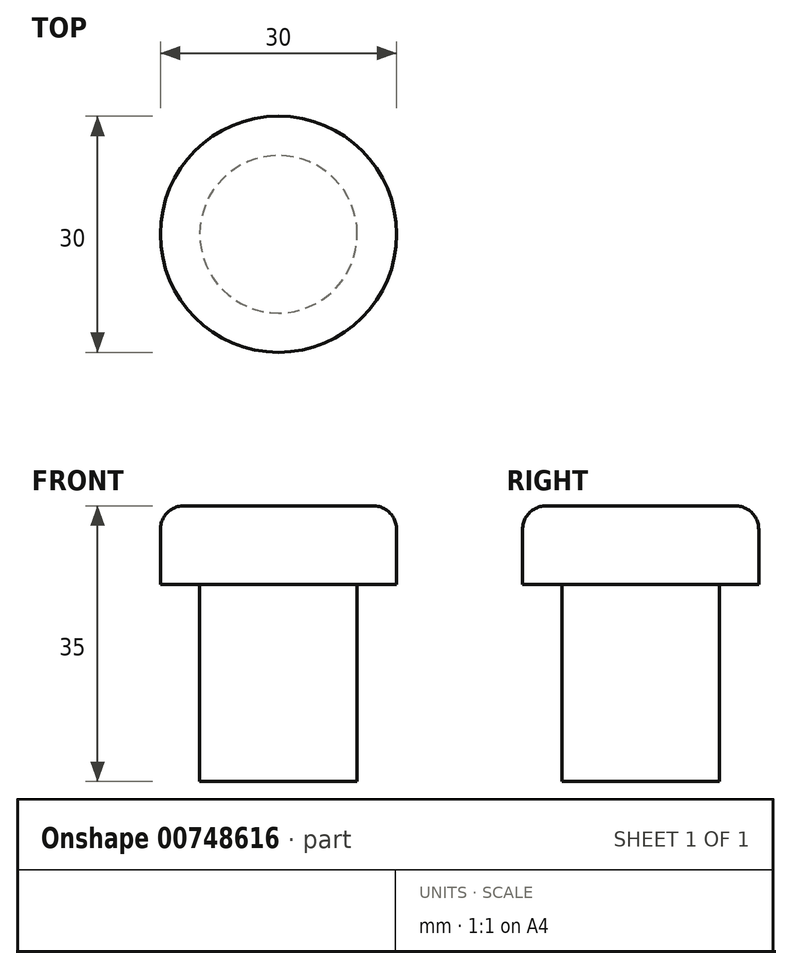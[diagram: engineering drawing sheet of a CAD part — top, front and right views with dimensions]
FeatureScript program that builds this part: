
annotation { "Feature Type Name" : "Feature", "Feature Type Description" : "" }
export const myFeature = defineFeature(function(context is Context, id is Id, definition is map)
    precondition{}
    {
        {
            var Q0;
            Q0=qCreatedBy(makeId("Top.planeOp"),FACE);
            var sketch = newSketch(context, id + "F0", { "sketchPlane" : qUnion([Q0])});
            skCircle(sketch, "E0", {"center": v(0, 0) * mm, "radius": 10 * mm});
            skSolve(sketch);
        }
        {
            var Q0;
            Q0=qSketchRegion(id+"F0",true);
            extrude(context, id + "F1", {"entities" : qUnion([Q0]), "depth" : 25 * mm, "offsetDistance" : 25 * mm});
        }
        {
            var Q0;
            Q0=makeQuery(id+"F1.opExtrude","CAP_FACE",FACE,{"disambiguationData":[OSD([sQuery(id+"F0.wireOp",EDGE,"E0")])],"isStart":false});
            var sketch = newSketch(context, id + "F2", { "sketchPlane" : qUnion([Q0])});
            skCircle(sketch, "E1", {"center": v(0, 0) * mm, "radius": 15 * mm});
            skSolve(sketch);
        }
        {
            var Q0;
            Q0=qSketchRegion(id+"F2",true);
            extrude(context, id + "F3", {"entities" : qUnion([Q0]), "operationType" : NewBodyOperationType.ADD, "depth" : 10 * mm, "offsetDistance" : 25 * mm});
        }
        {
            var Q0;
            Q0=makeQuery(id+"F3.opExtrude","CAP_EDGE",EDGE,{"disambiguationData":[OSD([sQuery(id+"F2.wireOp",EDGE,"E1")])],"isStart":false});
            fillet(context, id + "F4", {"entities" : qUnion([Q0]), "radius" : 3 * mm, "tangentPropagation" : true, "allowEdgeOverflow" : false});
        }
    });
